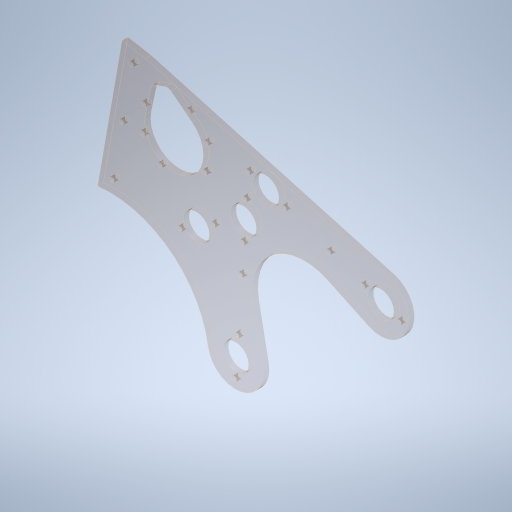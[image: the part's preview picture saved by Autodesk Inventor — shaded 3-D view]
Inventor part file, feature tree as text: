
AUTODESK INVENTOR PART (.ipt)
format: ipt  version: 2023.4 (Build 274418000, 418)  size: 430,080 bytes
history: native  units: in
note: dims shown in document units (in); Inventor stores cm internally (conversion verified against a paired STEP export)
features: sketch x3, extrude x2, hole x2, fillet x1, projected_geometry x1
ambient origin geometry x8: Origin, YZ Plane, XZ Plane, XY Plane, X Axis, Y Axis, Z Axis, Center Point
bodies: Solid1 (feature_tree)
feature tree (9):
  sketch  "Sketch1"  dims[d3=0.3489in d4=0.0in]
  extrude  "Extrusion1"  TaperAngle=0.0deg  [1 undecoded]
  hole  "Hole1"  [1 undecoded]
  hole  "Hole2"  [1 undecoded]
  extrude  "Extrusion2"  Depth=4.25in
  fillet  "Fillet1"  Radius=4.5in
  sketch  "Sketch2"  dims[d7=4.0in d8=4.0in]
  projected_geometry  "Projected Loop1"
  sketch  "Sketch3"  dims[d9=1.123in d10=4.0in d11=4.5in d12=4.5in d13=0.625in d14=0.625in d15=5.2115in d16=1.128in d17=5.2115in d18=1.8765in d19=1.8765in d22=1.0in d23=6.0in d26=10.0585in d27=2.5in d30=8.0in d31=0.0687in d32=0.75in d33=4.75in d34=1.375in d35=0.75in d36=0.25in d38=2.3622in d40=360.0deg d44=0.375in d45=0.25in d46=0.0in d47=0.201in d48=0.75in d49=0.37in d50=0.25in d51=90.0deg d52=1.0in d53=0.8108in d55=0.5497in d56=0.3in d58=2.256in d59=2.5in d60=2.9555in d61=2.35in d62=0.3779in d65=2.0in d66=2.3622in d68=360.0deg d70=1.625in d71=60.0deg d72=1.655in d73=0.201in d74=0.75in d75=0.385in d76=0.25in d77=0.5635in d78=1.0in d79=0.8108in d80=1.75in d82=0.75in d83=0.0in d84=0.0in d85=0.25in d86=1.5748in d88=360.0deg d91=1.5748in d93=360.0deg d95=45.0deg d96=0.25in d97=0.825in d98=4.25in]
note: 3 required parameter values undecoded (feature->parameter linkage not recoverable at this tier; creation-order binding heuristic only, values carry confidence <= 0.55)
